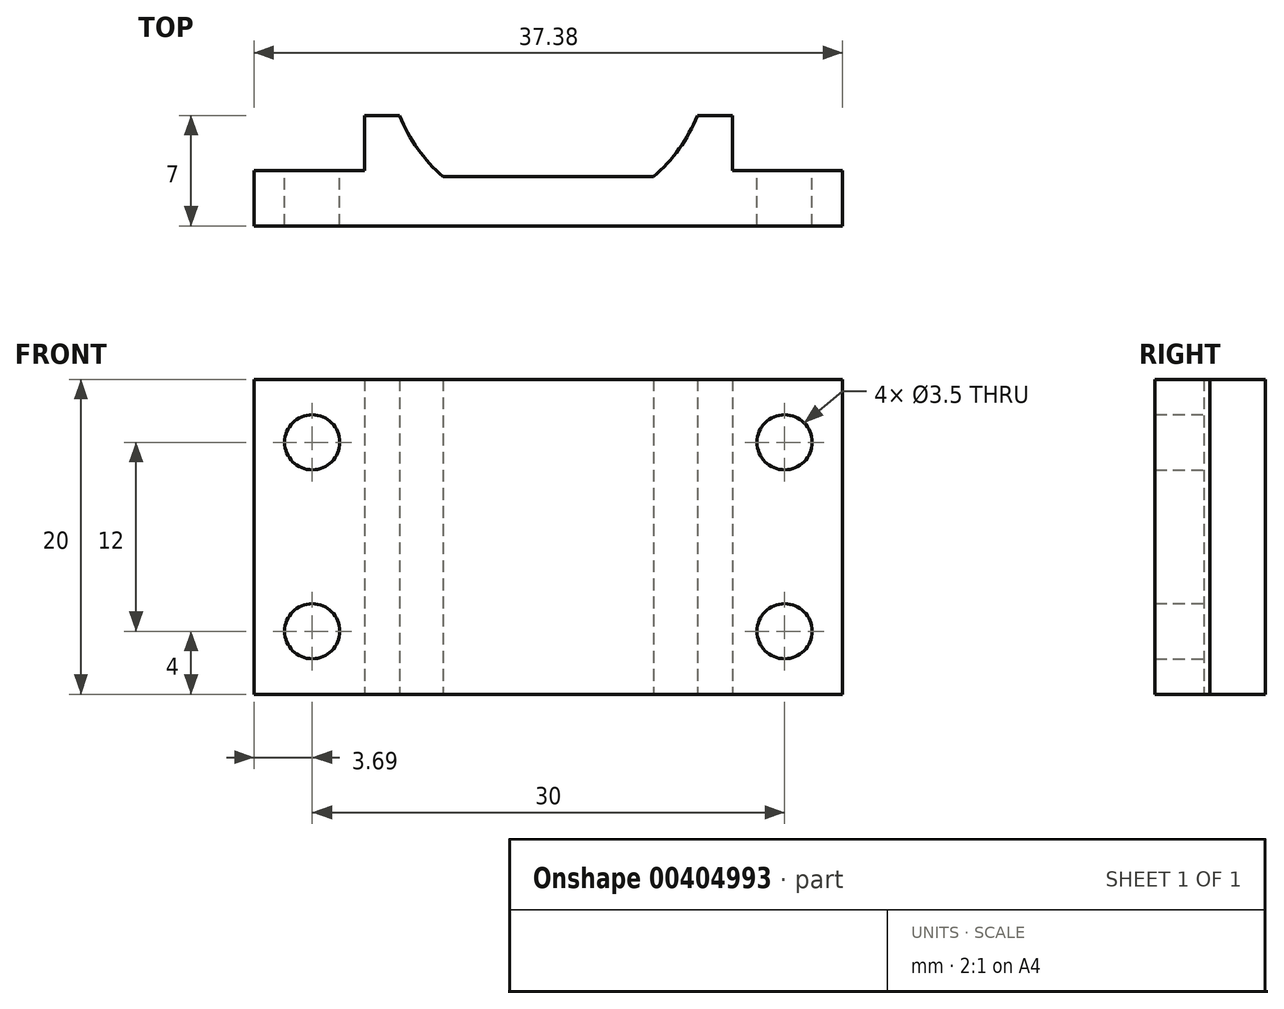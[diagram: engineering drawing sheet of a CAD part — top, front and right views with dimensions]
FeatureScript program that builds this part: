
annotation { "Feature Type Name" : "Feature", "Feature Type Description" : "" }
export const myFeature = defineFeature(function(context is Context, id is Id, definition is map)
    precondition{}
    {
        {
            var Q0;
            Q0=qCreatedBy(makeId("Top.planeOp"),FACE);
            var sketch = newSketch(context, id + "F0", { "sketchPlane" : qUnion([Q0])});
            skArc(sketch, "E0", {"start": v(-9.46, -3.82) * mm, "mid": v(-8.3, -5.93) * mm, "end": v(-6.69, -7.7) * mm});
            skLineSegment(sketch, "E1.top", {"start": v(-6.69, -7.7) * mm, "end": v(6.69, -7.7) * mm});
            skArc(sketch, "E2.trimOffspring", {"start": v(6.69, -7.7) * mm, "mid": v(8.3, -5.93) * mm, "end": v(9.46, -3.82) * mm});
            skLineSegment(sketch, "E3", {"start": v(-11.69, -7.32) * mm, "end": v(-18.69, -7.32) * mm});
            skLineSegment(sketch, "E4", {"start": v(-18.69, -7.32) * mm, "end": v(-18.69, -10.82) * mm});
            skLineSegment(sketch, "E5", {"start": v(-18.69, -10.82) * mm, "end": v(18.69, -10.82) * mm});
            skLineSegment(sketch, "E6", {"start": v(18.69, -10.82) * mm, "end": v(18.69, -7.32) * mm});
            skLineSegment(sketch, "E7", {"start": v(18.69, -7.32) * mm, "end": v(11.69, -7.32) * mm});
            skLineSegment(sketch, "E8", {"start": v(0, -10.82) * mm, "end": v(0, 0) * mm, "construction": true});
            skPoint(sketch, "E8.endSnap0", {"position": v(0, -7.7) * mm});
            skLineSegment(sketch, "E9", {"start": v(-11.69, -3.82) * mm, "end": v(-9.46, -3.82) * mm});
            skLineSegment(sketch, "E10", {"start": v(-11.69, -7.32) * mm, "end": v(-11.69, -3.82) * mm});
            skLineSegment(sketch, "E11", {"start": v(11.69, -7.32) * mm, "end": v(11.69, -3.82) * mm});
            skLineSegment(sketch, "E12.trimOffspring", {"start": v(9.46, -3.82) * mm, "end": v(11.69, -3.82) * mm});
            skSolve(sketch);
        }
        {
            var Q0;
            Q0=makeQuery(id+"F0.imprint","IMPRINT",FACE,{"disambiguationData":[TD([[makeQuery(id+"F0.imprint","IMPRINT",EDGE,{"derivedFrom":sQuery(id+"F0.wireOp",EDGE,"E0")}),-1.0]])]});
            extrude(context, id + "F1", {"entities" : qUnion([Q0]), "depth" : 20 * mm});
        }
        {
            var Q0;
            Q0=qSketchRegion(id+"F0",true);
            extrude(context, id + "F2", {"entities" : qUnion([Q0]), "operationType" : NewBodyOperationType.ADD, "depth" : 2 * mm});
        }
        {
            var Q0;
            Q0=makeQuery(id+"F1.opExtrude","SWEPT_FACE",FACE,{"disambiguationData":[OSD([sQuery(id+"F0.wireOp",EDGE,"E7")])]});
            var sketch = newSketch(context, id + "F3", { "sketchPlane" : qUnion([Q0])});
            skLineSegment(sketch, "E13", {"start": v(-15, 16) * mm, "end": v(-15, 4) * mm});
            skCircle(sketch, "E14", {"center": v(-15, 16) * mm, "radius": 1.75 * mm});
            skCircle(sketch, "E15", {"center": v(-15, 4) * mm, "radius": 1.75 * mm});
            skLineSegment(sketch, "E16", {"start": v(-15, 16) * mm, "end": v(15, 16) * mm});
            skLineSegment(sketch, "E17", {"start": v(-15, 4) * mm, "end": v(15, 4) * mm});
            skCircle(sketch, "E18", {"center": v(15, 16) * mm, "radius": 1.75 * mm});
            skCircle(sketch, "E19", {"center": v(15, 4) * mm, "radius": 1.75 * mm});
            skLineSegment(sketch, "E20", {"start": v(0, 4) * mm, "end": v(0, 0) * mm});
            skSolve(sketch);
        }
        {
            var Q0;
            Q0=qSketchRegion(id+"F3",true);
            extrude(context, id + "F4", {"entities" : qUnion([Q0]), "operationType" : NewBodyOperationType.REMOVE, "oppositeDirection" : true, "depth" : 25 * mm});
        }
    });
